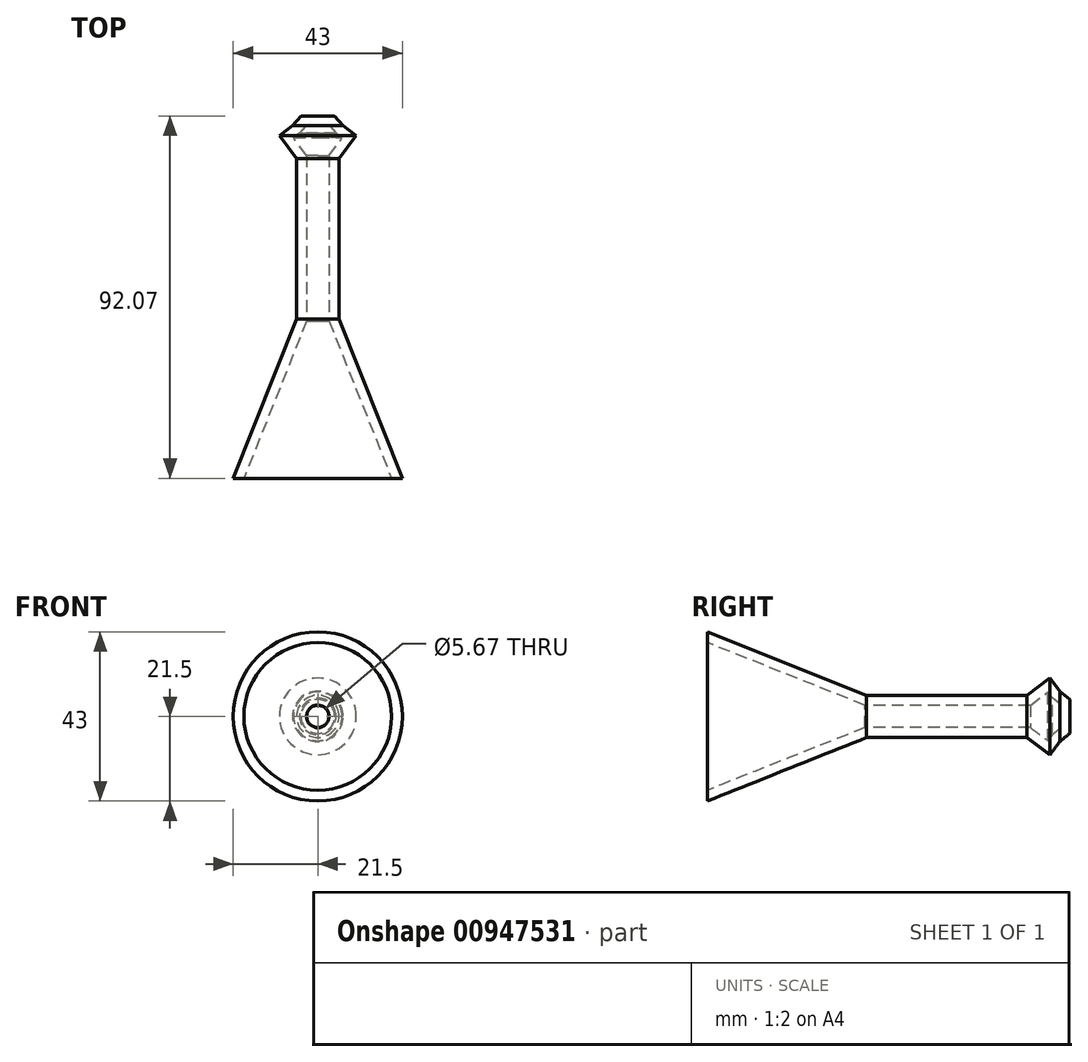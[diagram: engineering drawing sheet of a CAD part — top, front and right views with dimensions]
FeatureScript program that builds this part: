
annotation { "Feature Type Name" : "Feature", "Feature Type Description" : "" }
export const myFeature = defineFeature(function(context is Context, id is Id, definition is map)
    precondition{}
    {
        {
            var Q0;
            Q0=qCreatedBy(makeId("Top.planeOp"),FACE);
            var sketch = newSketch(context, id + "F0", { "sketchPlane" : qUnion([Q0])});
            skLineSegment(sketch, "E0", {"start": v(0, 51.6) * mm, "end": v(4.3, 51.6) * mm});
            skLineSegment(sketch, "E1", {"start": v(4.3, 51.6) * mm, "end": v(6.4, 49.08) * mm});
            skLineSegment(sketch, "E2", {"start": v(6.4, 49.08) * mm, "end": v(9.75, 46.56) * mm});
            skLineSegment(sketch, "E3", {"start": v(9.75, 46.56) * mm, "end": v(5.37, 40.72) * mm});
            skLineSegment(sketch, "E4", {"start": v(5.37, 40.72) * mm, "end": v(5.37, 0) * mm});
            skLineSegment(sketch, "E5", {"start": v(5.37, 0) * mm, "end": v(21.5, -40.48) * mm});
            skLineSegment(sketch, "E6", {"start": v(21.5, -40.48) * mm, "end": v(0, -40.48) * mm});
            skLineSegment(sketch, "E7", {"start": v(0, -40.48) * mm, "end": v(0, 51.6) * mm});
            skSolve(sketch);
        }
        {
            var Q0;
            Q0=makeQuery(id+"F0.imprint","IMPRINT",FACE,{"disambiguationData":[TD([[makeQuery(id+"F0.imprint","IMPRINT",EDGE,{"derivedFrom":sQuery(id+"F0.wireOp",EDGE,"E0")}),-1.0]])]});
            var Q1;
            Q1=sQuery(id+"F0.wireOp",EDGE,"E7");
            revolve(context, id + "F1", {"surfaceOperationType" : NewSurfaceOperationType.NEW, "entities" : qUnion([Q0]), "axis" : qUnion([Q1]), "revolveType" : RevolveType.FULL});
        }
        {
            var Q0;
            Q0=makeQuery(id+"F1.opRevolve","SWEPT_FACE",FACE,{"disambiguationData":[OSD([sQuery(id+"F0.wireOp",EDGE,"E6")])]});
            shell(context, id + "F2", {"entities" : qUnion([Q0]), "thickness" : 2.54 * mm});
        }
    });
